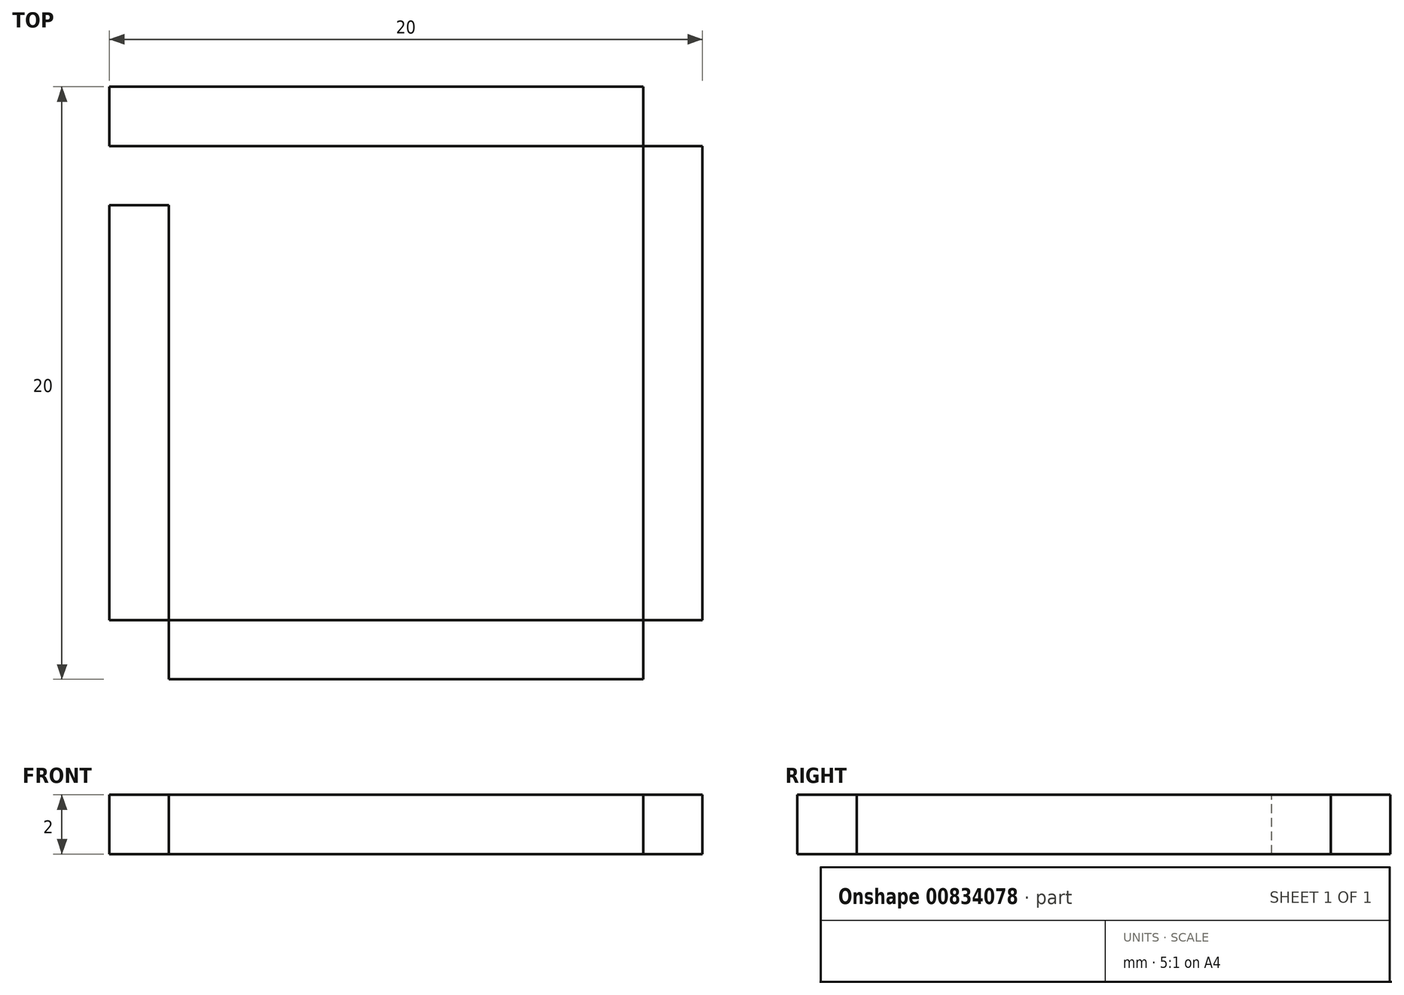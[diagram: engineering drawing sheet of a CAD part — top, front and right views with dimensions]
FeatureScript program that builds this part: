
annotation { "Feature Type Name" : "Feature", "Feature Type Description" : "" }
export const myFeature = defineFeature(function(context is Context, id is Id, definition is map)
    precondition{}
    {
        {
            var Q0;
            Q0=qCreatedBy(makeId("Top.planeOp"),FACE);
            var sketch = newSketch(context, id + "F0", { "sketchPlane" : qUnion([Q0])});
            skLineSegment(sketch, "E0.bottom", {"start": v(-10, -10) * mm, "end": v(10, -10) * mm});
            skLineSegment(sketch, "E0.top", {"start": v(-10, 10) * mm, "end": v(10, 10) * mm});
            skLineSegment(sketch, "E0.left", {"start": v(-10, -10) * mm, "end": v(-10, 10) * mm});
            skLineSegment(sketch, "E0.right", {"start": v(10, -10) * mm, "end": v(10, 10) * mm});
            skPoint(sketch, "E0.middle", {"position": v(0, 0) * mm});
            skLineSegment(sketch, "E1", {"start": v(-8, 10) * mm, "end": v(-8, -10) * mm});
            skLineSegment(sketch, "E2", {"start": v(-10, -8) * mm, "end": v(10, -8) * mm});
            skLineSegment(sketch, "E3", {"start": v(8, -10) * mm, "end": v(8, -8) * mm});
            skLineSegment(sketch, "E4", {"start": v(8, -8) * mm, "end": v(8, 10) * mm});
            skLineSegment(sketch, "E5", {"start": v(-10, 8) * mm, "end": v(10, 8) * mm});
            skSolve(sketch);
        }
        {
            var Q0;
            Q0 = qSketchRegion(id + "F0", true);
            var Q1;
            {var subQ0=sQuery(id+"F0.wireOp",EDGE,"E5");var subQ1=sQuery(id+"F0.wireOp",EDGE,"E1");var subQ2=makeQuery(id+"F0.imprint","INTERSECT",VERTEX,{"derivedFrom":[subQ1,subQ0]});Q1=makeQuery(id+"F0.imprint","IMPRINT",FACE,{"disambiguationData":[TD([[makeQuery(id+"F0.imprint","IMPRINT",EDGE,{"disambiguationData":[TD([[subQ2,-1.0]])],"derivedFrom":subQ1}),1.0]])]});}
            extrude(context, id + "F1", {"entities" : qUnion([Q0, Q1]), "depth" : 2 * mm, "offsetDistance" : 25 * mm});
        }
        {
            var Q0;
            Q0=makeQuery(id+"F1.opExtrude","CAP_FACE",FACE,{"disambiguationData":[OSD([sQuery(id+"F0.wireOp",EDGE,"E0.bottom"),sQuery(id+"F0.wireOp",EDGE,"E0.top"),sQuery(id+"F0.wireOp",EDGE,"E0.left"),sQuery(id+"F0.wireOp",EDGE,"E0.right")])],"isStart":false});
            var sketch = newSketch(context, id + "F2", { "sketchPlane" : qUnion([Q0])});
            skLineSegment(sketch, "E6", {"start": v(-10, -10) * mm, "end": v(-8, -10) * mm});
            skLineSegment(sketch, "E7", {"start": v(10, -10) * mm, "end": v(10, -8) * mm});
            skLineSegment(sketch, "E8", {"start": v(-8, -10) * mm, "end": v(-8, 10) * mm});
            skLineSegment(sketch, "E9", {"start": v(10, -8) * mm, "end": v(-10, -8) * mm});
            skLineSegment(sketch, "E10", {"start": v(10, -10) * mm, "end": v(8, -10) * mm});
            skLineSegment(sketch, "E11", {"start": v(8, 10) * mm, "end": v(8, -10) * mm});
            skLineSegment(sketch, "E12", {"start": v(-8, 10) * mm, "end": v(-8, 8) * mm});
            skLineSegment(sketch, "E13", {"start": v(-8, 8) * mm, "end": v(10, 8) * mm});
            skLineSegment(sketch, "E14", {"start": v(-8, 8) * mm, "end": v(-10, 8) * mm});
            skLineSegment(sketch, "E15", {"start": v(-8, 8) * mm, "end": v(-8, 6) * mm});
            skLineSegment(sketch, "E16", {"start": v(-8, 6) * mm, "end": v(-8, 4) * mm});
            skLineSegment(sketch, "E17", {"start": v(-8, 4) * mm, "end": v(-8, -4) * mm});
            skLineSegment(sketch, "E18", {"start": v(-8, -4) * mm, "end": v(-8, -6) * mm});
            skLineSegment(sketch, "E19", {"start": v(-8, -6) * mm, "end": v(-8, -8) * mm});
            skLineSegment(sketch, "E20", {"start": v(8, 8) * mm, "end": v(8, 6) * mm});
            skLineSegment(sketch, "E21", {"start": v(8, 6) * mm, "end": v(8, 4) * mm});
            skLineSegment(sketch, "E22", {"start": v(8, 4) * mm, "end": v(8, -4) * mm});
            skLineSegment(sketch, "E23", {"start": v(8, -4) * mm, "end": v(8, -6) * mm});
            skLineSegment(sketch, "E24", {"start": v(8, -6) * mm, "end": v(8, -8) * mm});
            skLineSegment(sketch, "E25", {"start": v(-8, -8) * mm, "end": v(-6, -8) * mm});
            skLineSegment(sketch, "E26", {"start": v(-6, -8) * mm, "end": v(-4, -8) * mm});
            skLineSegment(sketch, "E27", {"start": v(-4, -8) * mm, "end": v(4, -8) * mm});
            skLineSegment(sketch, "E28", {"start": v(4, -8) * mm, "end": v(6, -8) * mm});
            skLineSegment(sketch, "E29", {"start": v(6, -8) * mm, "end": v(8, -8) * mm});
            skLineSegment(sketch, "E30", {"start": v(-8, 6) * mm, "end": v(-10, 6) * mm});
            skLineSegment(sketch, "E31", {"start": v(-8, 4) * mm, "end": v(-10, 4) * mm});
            skLineSegment(sketch, "E32", {"start": v(-8, -4) * mm, "end": v(-10, -4) * mm});
            skLineSegment(sketch, "E33", {"start": v(-8, -6) * mm, "end": v(-10, -6) * mm});
            skLineSegment(sketch, "E34", {"start": v(-6, -8) * mm, "end": v(-6, -10) * mm});
            skLineSegment(sketch, "E35", {"start": v(-4, -8) * mm, "end": v(-4, -10) * mm});
            skLineSegment(sketch, "E36", {"start": v(4, -8) * mm, "end": v(4, -10) * mm});
            skLineSegment(sketch, "E37", {"start": v(6, -8) * mm, "end": v(6, -10) * mm});
            skLineSegment(sketch, "E38", {"start": v(8, -6) * mm, "end": v(10, -6) * mm});
            skLineSegment(sketch, "E39", {"start": v(8, -4) * mm, "end": v(10, -4) * mm});
            skLineSegment(sketch, "E40", {"start": v(8, 4) * mm, "end": v(10, 4) * mm});
            skLineSegment(sketch, "E41", {"start": v(8, 6) * mm, "end": v(10, 6) * mm});
            skSolve(sketch);
        }
        {
            var Q0;
            {var subQ0=sQuery(id+"F2.wireOp",EDGE,"E12");Q0=makeQuery(id+"F2.imprint","IMPRINT",FACE,{"disambiguationData":[TD([[makeQuery(id+"F2.imprint","IMPRINT",EDGE,{"derivedFrom":subQ0}),-1.0]])]});}
            var Q1;
            {var subQ0=sQuery(id+"F2.wireOp",EDGE,"E14");Q1=makeQuery(id+"F2.imprint","IMPRINT",FACE,{"disambiguationData":[TD([[makeQuery(id+"F2.imprint","IMPRINT",EDGE,{"derivedFrom":subQ0}),1.0]])]});}
            var Q2;
            Q2=makeQuery(id+"F2.imprint","IMPRINT",FACE,{"disambiguationData":[TD([[makeQuery(id+"F2.imprint","IMPRINT",EDGE,{"derivedFrom":sQuery(id+"F2.wireOp",EDGE,"E17")}),-1.0]])]});
            var Q3;
            {var subQ0=sQuery(id+"F2.wireOp",EDGE,"E19");Q3=makeQuery(id+"F2.imprint","IMPRINT",FACE,{"disambiguationData":[TD([[makeQuery(id+"F2.imprint","IMPRINT",EDGE,{"derivedFrom":subQ0}),-1.0]])]});}
            var Q4;
            {var subQ0=sQuery(id+"F2.wireOp",EDGE,"E6");Q4=makeQuery(id+"F2.imprint","IMPRINT",FACE,{"disambiguationData":[TD([[makeQuery(id+"F2.imprint","IMPRINT",EDGE,{"derivedFrom":subQ0}),1.0]])]});}
            var Q5;
            {var subQ0=sQuery(id+"F2.wireOp",EDGE,"E8");Q5=makeQuery(id+"F2.imprint","IMPRINT",FACE,{"disambiguationData":[TD([[makeQuery(id+"F2.imprint","IMPRINT",EDGE,{"derivedFrom":subQ0}),-1.0]])]});}
            var Q6;
            Q6=makeQuery(id+"F2.imprint","IMPRINT",FACE,{"disambiguationData":[TD([[makeQuery(id+"F2.imprint","IMPRINT",EDGE,{"derivedFrom":sQuery(id+"F2.wireOp",EDGE,"E27")}),-1.0]])]});
            var Q7;
            {var subQ3=sQuery(id+"F2.wireOp",EDGE,"E29");Q7=makeQuery(id+"F2.imprint","IMPRINT",FACE,{"disambiguationData":[TD([[makeQuery(id+"F2.imprint","IMPRINT",EDGE,{"derivedFrom":subQ3}),-1.0]])]});}
            var Q8;
            {var subQ0=sQuery(id+"F2.wireOp",EDGE,"E7");Q8=makeQuery(id+"F2.imprint","IMPRINT",FACE,{"disambiguationData":[TD([[makeQuery(id+"F2.imprint","IMPRINT",EDGE,{"derivedFrom":subQ0}),1.0]])]});}
            var Q9;
            {var subQ3=sQuery(id+"F2.wireOp",EDGE,"E24");Q9=makeQuery(id+"F2.imprint","IMPRINT",FACE,{"disambiguationData":[TD([[makeQuery(id+"F2.imprint","IMPRINT",EDGE,{"derivedFrom":subQ3}),1.0]])]});}
            var Q10;
            Q10=makeQuery(id+"F2.imprint","IMPRINT",FACE,{"disambiguationData":[TD([[makeQuery(id+"F2.imprint","IMPRINT",EDGE,{"derivedFrom":sQuery(id+"F2.wireOp",EDGE,"E22")}),1.0]])]});
            var Q11;
            {var subQ3=sQuery(id+"F2.wireOp",EDGE,"E20");Q11=makeQuery(id+"F2.imprint","IMPRINT",FACE,{"disambiguationData":[TD([[makeQuery(id+"F2.imprint","IMPRINT",EDGE,{"derivedFrom":subQ3}),1.0]])]});}
            var Q12;
            {var subQ1=makeQuery(id+"F1.opExtrude","CAP_EDGE",EDGE,{"disambiguationData":[OSD([sQuery(id+"F0.wireOp",EDGE,"E0.top")])],"isStart":false});var subQ5=makeQuery(id+"F1.opExtrude","CAP_EDGE",EDGE,{"disambiguationData":[OSD([sQuery(id+"F0.wireOp",EDGE,"E0.right")])],"isStart":false});var subQ7=makeQuery(id+"F2.imprint","INTERSECT",VERTEX,{"derivedFrom":[subQ1,subQ5]});Q12=makeQuery(id+"F2.imprint","IMPRINT",FACE,{"disambiguationData":[TD([[makeQuery(id+"F2.imprint","IMPRINT",EDGE,{"disambiguationData":[TD([[subQ7,1.0]])],"derivedFrom":subQ1}),-1.0]])]});}
            extrude(context, id + "F3", {"entities" : qUnion([Q0, Q1, Q2, Q3, Q4, Q5, Q6, Q7, Q8, Q9, Q10, Q11, Q12]), "operationType" : NewBodyOperationType.REMOVE, "oppositeDirection" : true, "depth" : 25 * mm, "offsetDistance" : 25 * mm});
        }
    });
